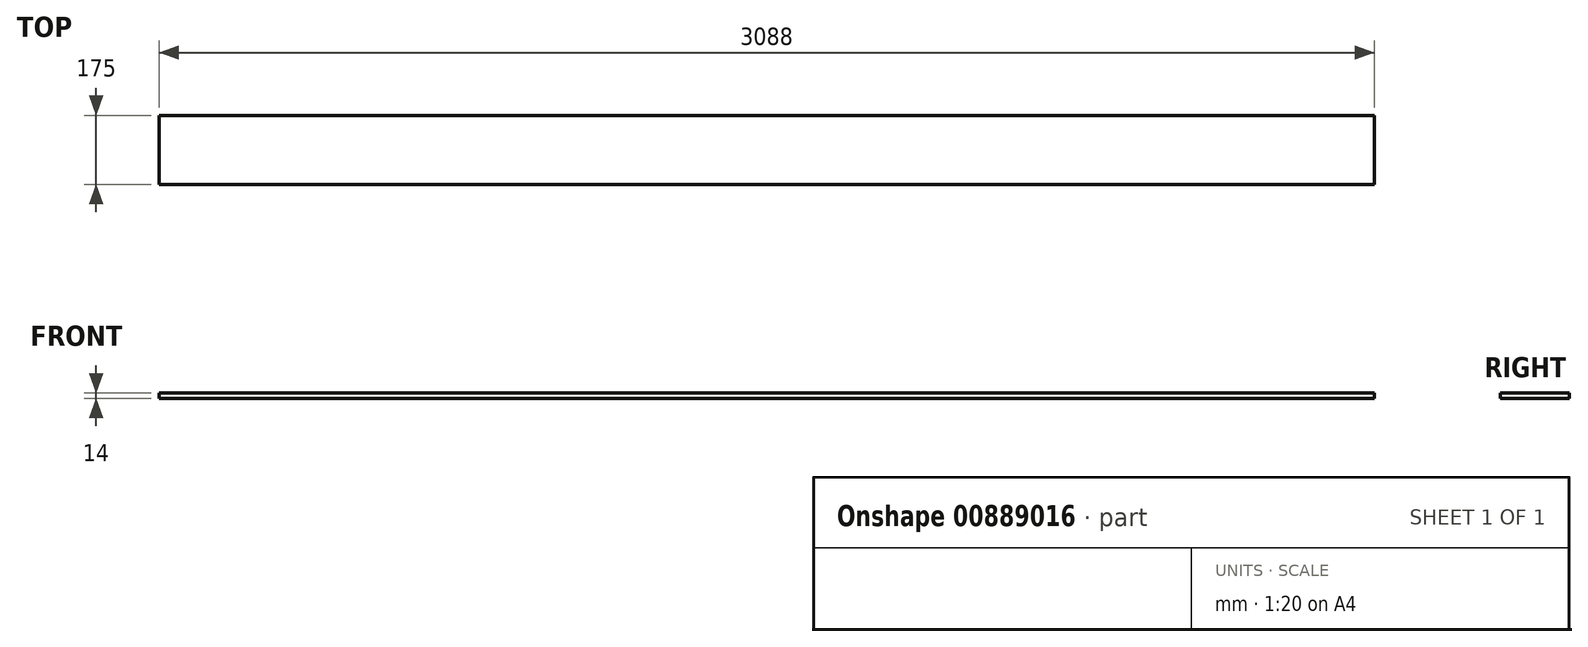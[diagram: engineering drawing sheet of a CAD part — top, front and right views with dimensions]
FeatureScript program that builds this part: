
annotation { "Feature Type Name" : "Feature", "Feature Type Description" : "" }
export const myFeature = defineFeature(function(context is Context, id is Id, definition is map)
    precondition{}
    {
        {
            var Q0;
            Q0=qCreatedBy(makeId("Top.planeOp"),FACE);
            var sketch = newSketch(context, id + "F0", { "sketchPlane" : qUnion([Q0])});
            skLineSegment(sketch, "E0.bottom", {"start": v(-1544, 87.5) * mm, "end": v(1544, 87.5) * mm});
            skLineSegment(sketch, "E0.top", {"start": v(-1544, -87.5) * mm, "end": v(1544, -87.5) * mm});
            skLineSegment(sketch, "E0.left", {"start": v(-1544, 87.5) * mm, "end": v(-1544, -87.5) * mm});
            skLineSegment(sketch, "E0.right", {"start": v(1544, 87.5) * mm, "end": v(1544, -87.5) * mm});
            skPoint(sketch, "E0.middle", {"position": v(0, 0) * mm});
            skSolve(sketch);
        }
        {
            var Q0;
            Q0 = qSketchRegion(id + "F0", true);
            extrude(context, id + "F1", {"entities" : qUnion([Q0]), "depth" : 14 * mm, "offsetDistance" : 25 * mm});
        }
    });
